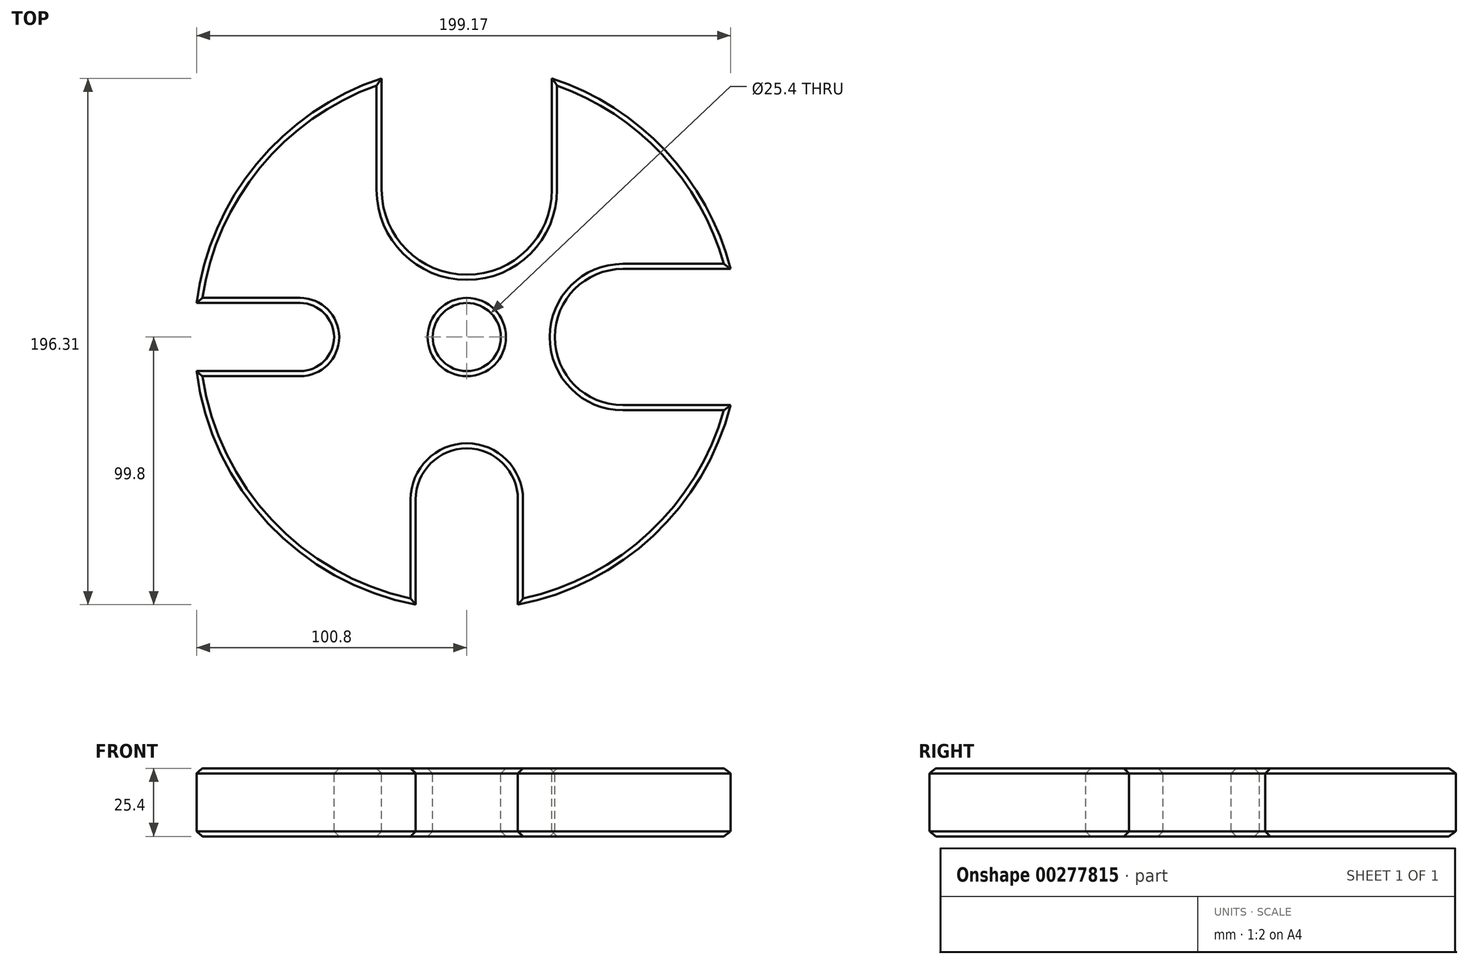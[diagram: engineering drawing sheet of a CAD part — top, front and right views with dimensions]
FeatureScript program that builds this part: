
annotation { "Feature Type Name" : "Feature", "Feature Type Description" : "" }
export const myFeature = defineFeature(function(context is Context, id is Id, definition is map)
    precondition{}
    {
        {
            var Q0;
            Q0=qCreatedBy(makeId("Top.planeOp"),FACE);
            var sketch = newSketch(context, id + "F0", { "sketchPlane" : qUnion([Q0])});
            skArc(sketch, "E0", {"start": v(-31.75, 96.51) * mm, "mid": v(-78.41, 64.6) * mm, "end": v(-100.8, 12.7) * mm});
            skCircle(sketch, "E1", {"center": v(0, 0) * mm, "radius": 63.5 * mm, "construction": true});
            skLineSegment(sketch, "E2", {"start": v(0, 101.6) * mm, "end": v(0, -101.6) * mm, "construction": true});
            skLineSegment(sketch, "E3", {"start": v(-101.6, 0) * mm, "end": v(101.6, 0) * mm, "construction": true});
            skCircle(sketch, "E4", {"center": v(0, 0) * mm, "radius": 12.7 * mm});
            skLineSegment(sketch, "E5", {"start": v(-100.8, 12.7) * mm, "end": v(-62.22, 12.7) * mm});
            skLineSegment(sketch, "E6", {"start": v(-100.8, -12.7) * mm, "end": v(-62.22, -12.7) * mm});
            skLineSegment(sketch, "E7", {"start": v(-31.75, 96.51) * mm, "end": v(-31.75, 55) * mm});
            skLineSegment(sketch, "E8", {"start": v(31.75, 96.51) * mm, "end": v(31.75, 55) * mm});
            skLineSegment(sketch, "E9", {"start": v(58.2, 25.4) * mm, "end": v(98.37, 25.4) * mm});
            skLineSegment(sketch, "E10", {"start": v(58.2, -25.4) * mm, "end": v(98.37, -25.4) * mm});
            skLineSegment(sketch, "E11", {"start": v(-19.05, -60.58) * mm, "end": v(-19.05, -99.8) * mm});
            skLineSegment(sketch, "E12", {"start": v(19.05, -60.58) * mm, "end": v(19.05, -99.8) * mm});
            skArc(sketch, "E13", {"start": v(-62.22, 12.7) * mm, "mid": v(-49.52, 0) * mm, "end": v(-62.22, -12.7) * mm});
            skArc(sketch, "E14", {"start": v(-19.05, -60.58) * mm, "mid": v(0, -41.53) * mm, "end": v(19.05, -60.58) * mm});
            skArc(sketch, "E15", {"start": v(58.2, -25.4) * mm, "mid": v(32.8, 0) * mm, "end": v(58.2, 25.4) * mm});
            skArc(sketch, "E16", {"start": v(31.75, 55) * mm, "mid": v(0, 23.24) * mm, "end": v(-31.75, 55) * mm});
            skArc(sketch, "E17.trimOffspring", {"start": v(98.37, 25.4) * mm, "mid": v(74.14, 69.46) * mm, "end": v(31.75, 96.51) * mm});
            skArc(sketch, "E18.trimOffspring", {"start": v(19.05, -99.8) * mm, "mid": v(69.5, -74.1) * mm, "end": v(98.37, -25.4) * mm});
            skArc(sketch, "E19.trimOffspring", {"start": v(-100.8, -12.7) * mm, "mid": v(-74.08, -69.53) * mm, "end": v(-19.05, -99.8) * mm});
            skSolve(sketch);
        }
        {
            var Q0;
            Q0=makeQuery(id+"F0.imprint","IMPRINT",FACE,{"disambiguationData":[TD([[makeQuery(id+"F0.imprint","IMPRINT",EDGE,{"derivedFrom":sQuery(id+"F0.wireOp",EDGE,"E0")}),1.0]])]});
            extrude(context, id + "F1", {"entities" : qUnion([Q0]), "oppositeDirection" : true, "depth" : 25.4 * mm});
        }
        {
            var Q0;
            Q0=makeQuery(id+"F1.opExtrude","CAP_FACE",FACE,{"disambiguationData":[OSD([sQuery(id+"F0.wireOp",EDGE,"E0"),sQuery(id+"F0.wireOp",EDGE,"E4"),sQuery(id+"F0.wireOp",EDGE,"E5"),sQuery(id+"F0.wireOp",EDGE,"E6"),sQuery(id+"F0.wireOp",EDGE,"E7"),sQuery(id+"F0.wireOp",EDGE,"E8"),sQuery(id+"F0.wireOp",EDGE,"E9"),sQuery(id+"F0.wireOp",EDGE,"E10"),sQuery(id+"F0.wireOp",EDGE,"E11"),sQuery(id+"F0.wireOp",EDGE,"E12"),sQuery(id+"F0.wireOp",EDGE,"E13"),sQuery(id+"F0.wireOp",EDGE,"E14"),sQuery(id+"F0.wireOp",EDGE,"E15"),sQuery(id+"F0.wireOp",EDGE,"E16"),sQuery(id+"F0.wireOp",EDGE,"E17.trimOffspring"),sQuery(id+"F0.wireOp",EDGE,"E18.trimOffspring"),sQuery(id+"F0.wireOp",EDGE,"E19.trimOffspring")])],"isStart":true});
            var Q1;
            Q1=makeQuery(id+"F1.opExtrude","CAP_FACE",FACE,{"disambiguationData":[OSD([sQuery(id+"F0.wireOp",EDGE,"E0"),sQuery(id+"F0.wireOp",EDGE,"E4"),sQuery(id+"F0.wireOp",EDGE,"E5"),sQuery(id+"F0.wireOp",EDGE,"E6"),sQuery(id+"F0.wireOp",EDGE,"E7"),sQuery(id+"F0.wireOp",EDGE,"E8"),sQuery(id+"F0.wireOp",EDGE,"E9"),sQuery(id+"F0.wireOp",EDGE,"E10"),sQuery(id+"F0.wireOp",EDGE,"E11"),sQuery(id+"F0.wireOp",EDGE,"E12"),sQuery(id+"F0.wireOp",EDGE,"E13"),sQuery(id+"F0.wireOp",EDGE,"E14"),sQuery(id+"F0.wireOp",EDGE,"E15"),sQuery(id+"F0.wireOp",EDGE,"E16"),sQuery(id+"F0.wireOp",EDGE,"E17.trimOffspring"),sQuery(id+"F0.wireOp",EDGE,"E18.trimOffspring"),sQuery(id+"F0.wireOp",EDGE,"E19.trimOffspring")])],"isStart":false});
            chamfer(context, id + "F2", {"entities" : qUnion([Q0, Q1]), "chamferType" : ChamferType.OFFSET_ANGLE, "width" : 1.9 * mm, "oppositeDirection" : false, "angle" : 45 * degree, "tangentPropagation" : true});
        }
    });
